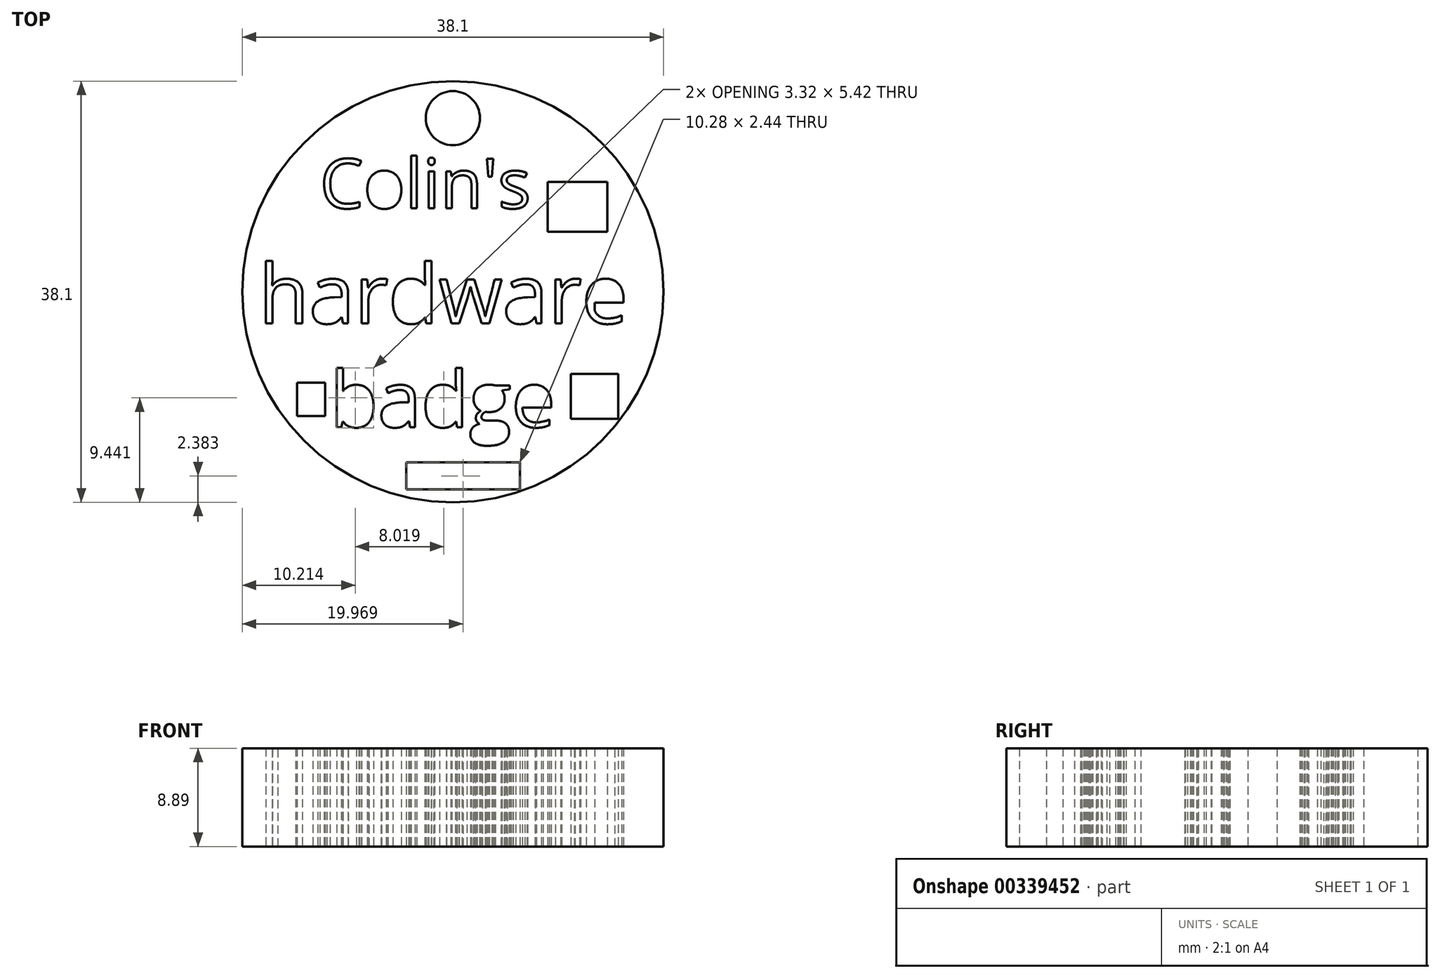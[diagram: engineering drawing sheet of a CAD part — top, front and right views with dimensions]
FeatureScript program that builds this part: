
annotation { "Feature Type Name" : "Feature", "Feature Type Description" : "" }
export const myFeature = defineFeature(function(context is Context, id is Id, definition is map)
    precondition{}
    {
        {
            var Q0;
            Q0=qCreatedBy(makeId("Top.planeOp"),FACE);
            var sketch = newSketch(context, id + "F0", { "sketchPlane" : qUnion([Q0])});
            skCircle(sketch, "E0", {"center": v(0, 0) * mm, "radius": 19.05 * mm});
            skText(sketch, "E1", { "text": "Colin\'s\n", "fontName": "OpenSans-Regular.ttf"});
            skText(sketch, "E2", { "text": "hardware", "fontName": "OpenSans-Regular.ttf"});
            skText(sketch, "E3", { "text": "badge", "fontName": "OpenSans-Regular.ttf"});
            skLineSegment(sketch, "E4.bottom", {"start": v(-12.83, 14.08) * mm, "end": v(12.83, 14.08) * mm});
            skLineSegment(sketch, "E4.top", {"start": v(-12.83, -14.08) * mm, "end": v(12.83, -14.08) * mm});
            skLineSegment(sketch, "E4.left", {"start": v(-12.83, 14.08) * mm, "end": v(-12.83, -14.08) * mm});
            skLineSegment(sketch, "E4.right", {"start": v(12.83, 14.08) * mm, "end": v(12.83, -14.08) * mm});
            skLineSegment(sketch, "E5.bottom", {"start": v(14.97, -7.44) * mm, "end": v(10.69, -7.44) * mm});
            skLineSegment(sketch, "E5.top", {"start": v(14.97, -11.51) * mm, "end": v(10.69, -11.51) * mm});
            skLineSegment(sketch, "E5.left", {"start": v(14.97, -7.44) * mm, "end": v(14.97, -11.51) * mm});
            skLineSegment(sketch, "E5.right", {"start": v(10.69, -7.44) * mm, "end": v(10.69, -11.51) * mm});
            skPoint(sketch, "E5.middle", {"position": v(12.83, -9.48) * mm});
            skLineSegment(sketch, "E6.bottom", {"start": v(-14.1, -8.23) * mm, "end": v(-11.56, -8.23) * mm});
            skLineSegment(sketch, "E6.top", {"start": v(-14.1, -11.24) * mm, "end": v(-11.56, -11.24) * mm});
            skLineSegment(sketch, "E6.left", {"start": v(-14.1, -8.23) * mm, "end": v(-14.1, -11.24) * mm});
            skLineSegment(sketch, "E6.right", {"start": v(-11.56, -8.23) * mm, "end": v(-11.56, -11.24) * mm});
            skPoint(sketch, "E6.middle", {"position": v(-12.83, -9.74) * mm});
            skCircle(sketch, "E7", {"center": v(0, 15.7) * mm, "radius": 2.45 * mm});
            skLineSegment(sketch, "E8.bottom", {"start": v(-4.22, -15.45) * mm, "end": v(6.06, -15.45) * mm});
            skLineSegment(sketch, "E8.top", {"start": v(-4.22, -17.89) * mm, "end": v(6.06, -17.89) * mm});
            skLineSegment(sketch, "E8.left", {"start": v(-4.22, -15.45) * mm, "end": v(-4.22, -17.89) * mm});
            skLineSegment(sketch, "E8.right", {"start": v(6.06, -15.45) * mm, "end": v(6.06, -17.89) * mm});
            skPoint(sketch, "E8.middle", {"position": v(0.92, -16.67) * mm});
            skLineSegment(sketch, "E9.bottom", {"start": v(13.97, 9.94) * mm, "end": v(8.57, 9.94) * mm});
            skLineSegment(sketch, "E9.top", {"start": v(13.97, 5.42) * mm, "end": v(8.57, 5.42) * mm});
            skLineSegment(sketch, "E9.left", {"start": v(13.97, 9.94) * mm, "end": v(13.97, 5.42) * mm});
            skLineSegment(sketch, "E9.right", {"start": v(8.57, 9.94) * mm, "end": v(8.57, 5.42) * mm});
            skPoint(sketch, "E9.middle", {"position": v(11.27, 7.68) * mm});
            const initialGuessF0  = {"E1": [-0.01203, 0.00755, 1, 0, 0.0045], "E2": [-0.01757, -0.00287, 1, 0, 0.00535], "E3": [-0.0111, -0.01225, 1, 0, 0.00507]};
            skSetInitialGuess(sketch, initialGuessF0);
            skSolve(sketch);
        }
        {
            var Q0;
            Q0 = qSketchRegion(id + "F0", true);
            extrude(context, id + "F1", {"entities" : qUnion([Q0]), "depth" : 8.9 * mm});
        }
    });
